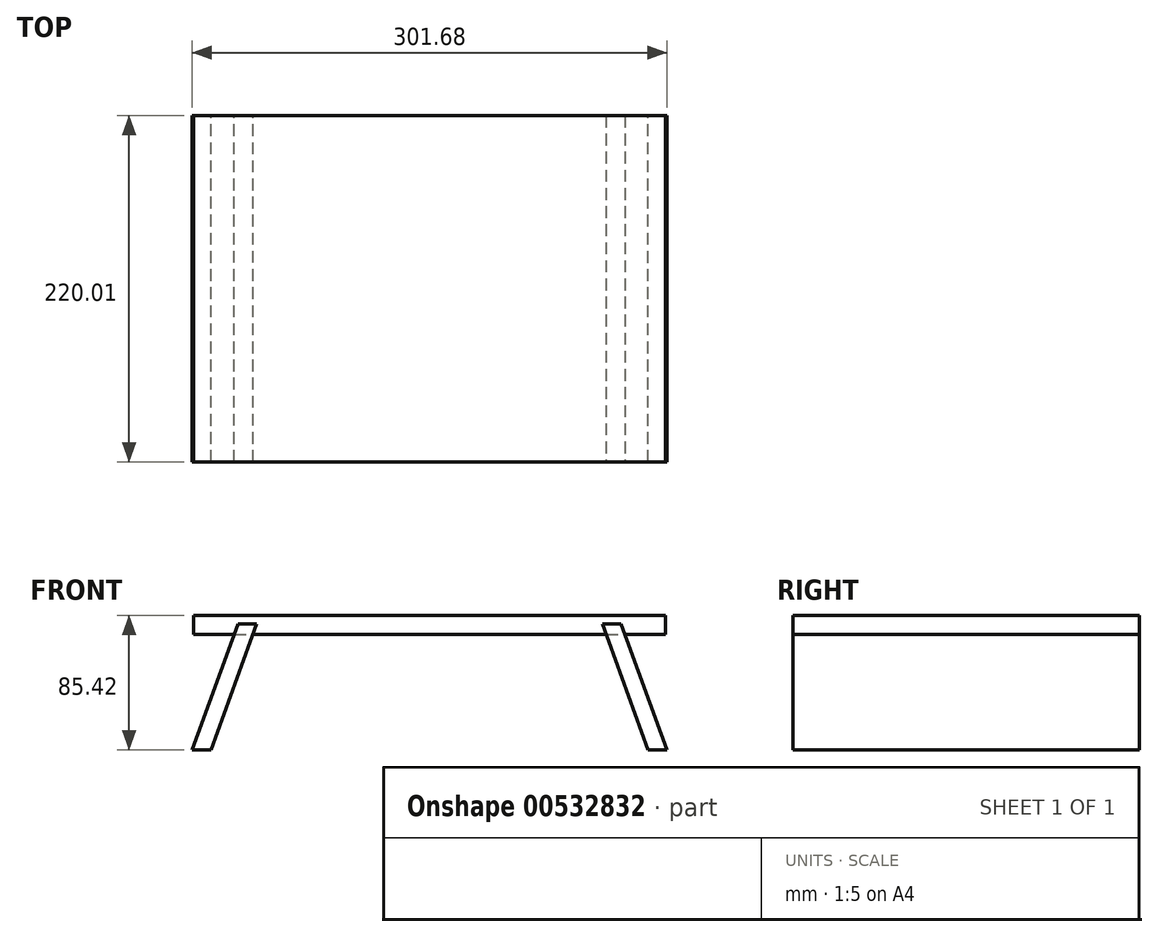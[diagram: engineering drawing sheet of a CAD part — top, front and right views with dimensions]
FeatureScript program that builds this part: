
annotation { "Feature Type Name" : "Feature", "Feature Type Description" : "" }
export const myFeature = defineFeature(function(context is Context, id is Id, definition is map)
    precondition{}
    {
        {
            var Q0;
            Q0=qCreatedBy(makeId("Top.planeOp"),FACE);
            var sketch = newSketch(context, id + "F0", { "sketchPlane" : qUnion([Q0])});
            skLineSegment(sketch, "E0.bottom", {"start": v(150, -110) * mm, "end": v(-150, -110) * mm});
            skLineSegment(sketch, "E0.top", {"start": v(150, 110) * mm, "end": v(-150, 110) * mm});
            skLineSegment(sketch, "E0.left", {"start": v(150, -110) * mm, "end": v(150, 110) * mm});
            skLineSegment(sketch, "E0.right", {"start": v(-150, -110) * mm, "end": v(-150, 110) * mm});
            skPoint(sketch, "E0.middle", {"position": v(0, 0) * mm});
            skSolve(sketch);
        }
        {
            var Q0;
            Q0=makeQuery(id+"F0.imprint","IMPRINT",FACE,{"disambiguationData":[TD([[makeQuery(id+"F0.imprint","IMPRINT",EDGE,{"derivedFrom":sQuery(id+"F0.wireOp",EDGE,"E0.bottom")}),-1.0]])]});
            extrude(context, id + "F1", {"entities" : qUnion([Q0]), "depth" : 12 * mm, "offsetDistance" : 25 * mm});
        }
        {
            var Q0;
            Q0=qCreatedBy(makeId("Front.planeOp"),FACE);
            var sketch = newSketch(context, id + "F2", { "sketchPlane" : qUnion([Q0])});
            skLineSegment(sketch, "E1.left", {"start": v(102.01, -89.83) * mm, "end": v(102.01, -4.7) * mm});
            skLineSegment(sketch, "E1.right", {"start": v(90.74, -85.72) * mm, "end": v(90.74, -0.59) * mm});
            skPoint(sketch, "E1.middle", {"position": v(96.37, -45.2) * mm});
            skLineSegment(sketch, "E2", {"start": v(90.74, -0.59) * mm, "end": v(90.74, -0.59) * mm});
            skLineSegment(sketch, "E3", {"start": v(90.74, -0.59) * mm, "end": v(102.01, -4.7) * mm});
            skPoint(sketch, "E4", {"position": v(102.01, -4.7) * mm});
            skLineSegment(sketch, "E5", {"start": v(90.74, -85.72) * mm, "end": v(102.01, -89.83) * mm});
            skSolve(sketch);
        }
        {
            var Q0;
            Q0=makeQuery(id+"F2.imprint","IMPRINT",FACE,{"disambiguationData":[TD([[makeQuery(id+"F2.imprint","IMPRINT",EDGE,{"derivedFrom":sQuery(id+"F2.wireOp",EDGE,"E1.bottom")}),-1.0]])]});
            var Q1;
            Q1=makeQuery(id+"F2.imprint","IMPRINT",FACE,{"disambiguationData":[TD([[makeQuery(id+"F2.imprint","IMPRINT",EDGE,{"derivedFrom":sQuery(id+"F2.wireOp",EDGE,"E1.left")}),1.0]])]});
            extrude(context, id + "F3", {"entities" : qUnion([Q0, Q1]), "depth" : 220 * mm, "offsetDistance" : 25 * mm});
        }
        {
            var Q0;
            Q0=makeQuery(id+"F3.opExtrude","SWEPT_BODY",BODY,{"disambiguationData":[OSD([sQuery(id+"F2.wireOp",EDGE,"E1.left"),sQuery(id+"F2.wireOp",EDGE,"E1.right"),sQuery(id+"F2.wireOp",EDGE,"E3"),sQuery(id+"F2.wireOp",EDGE,"E5")])]});
            var Q1;
            Q1=makeQuery(id+"F3.opExtrude","SWEPT_EDGE",EDGE,{"disambiguationData":[OSD([sQuery(id+"F2.wireOp",EDGE,"E1.right"),sQuery(id+"F2.wireOp",EDGE,"E5")])]});
            transform(context, id + "F4", {"entities" : qUnion([Q0]), "transformType" : TransformType.ROTATION, "transformAxis" : qUnion([Q1]), "angle" : 20 * degree, "oppositeDirection" : true, "makeCopy" : false});
        }
        {
            var Q0;
            Q0=makeQuery(id+"F3.opExtrude","SWEPT_BODY",BODY,{"disambiguationData":[OSD([sQuery(id+"F2.wireOp",EDGE,"E1.left"),sQuery(id+"F2.wireOp",EDGE,"E1.right"),sQuery(id+"F2.wireOp",EDGE,"E3"),sQuery(id+"F2.wireOp",EDGE,"E5")])]});
            transform(context, id + "F5", {"entities" : qUnion([Q0]), "transformType" : TransformType.TRANSLATION_3D, "dx" : 48.1 * mm, "dy" : 110 * mm, "dz" : 12.3 * mm, "makeCopy" : false});
        }
        {
            var Q0;
            Q0=makeQuery(id+"F3.opExtrude","SWEPT_BODY",BODY,{"disambiguationData":[OSD([sQuery(id+"F2.wireOp",EDGE,"E1.left"),sQuery(id+"F2.wireOp",EDGE,"E1.right"),sQuery(id+"F2.wireOp",EDGE,"E3"),sQuery(id+"F2.wireOp",EDGE,"E5")])]});
            var Q1;
            Q1=qCreatedBy(makeId("Right.planeOp"),FACE);
            mirror(context, id + "F6", {"operationType" : NewBodyOperationType.ADD, "entities" : qUnion([Q0]), "mirrorPlane" : qUnion([Q1])});
        }
    });
